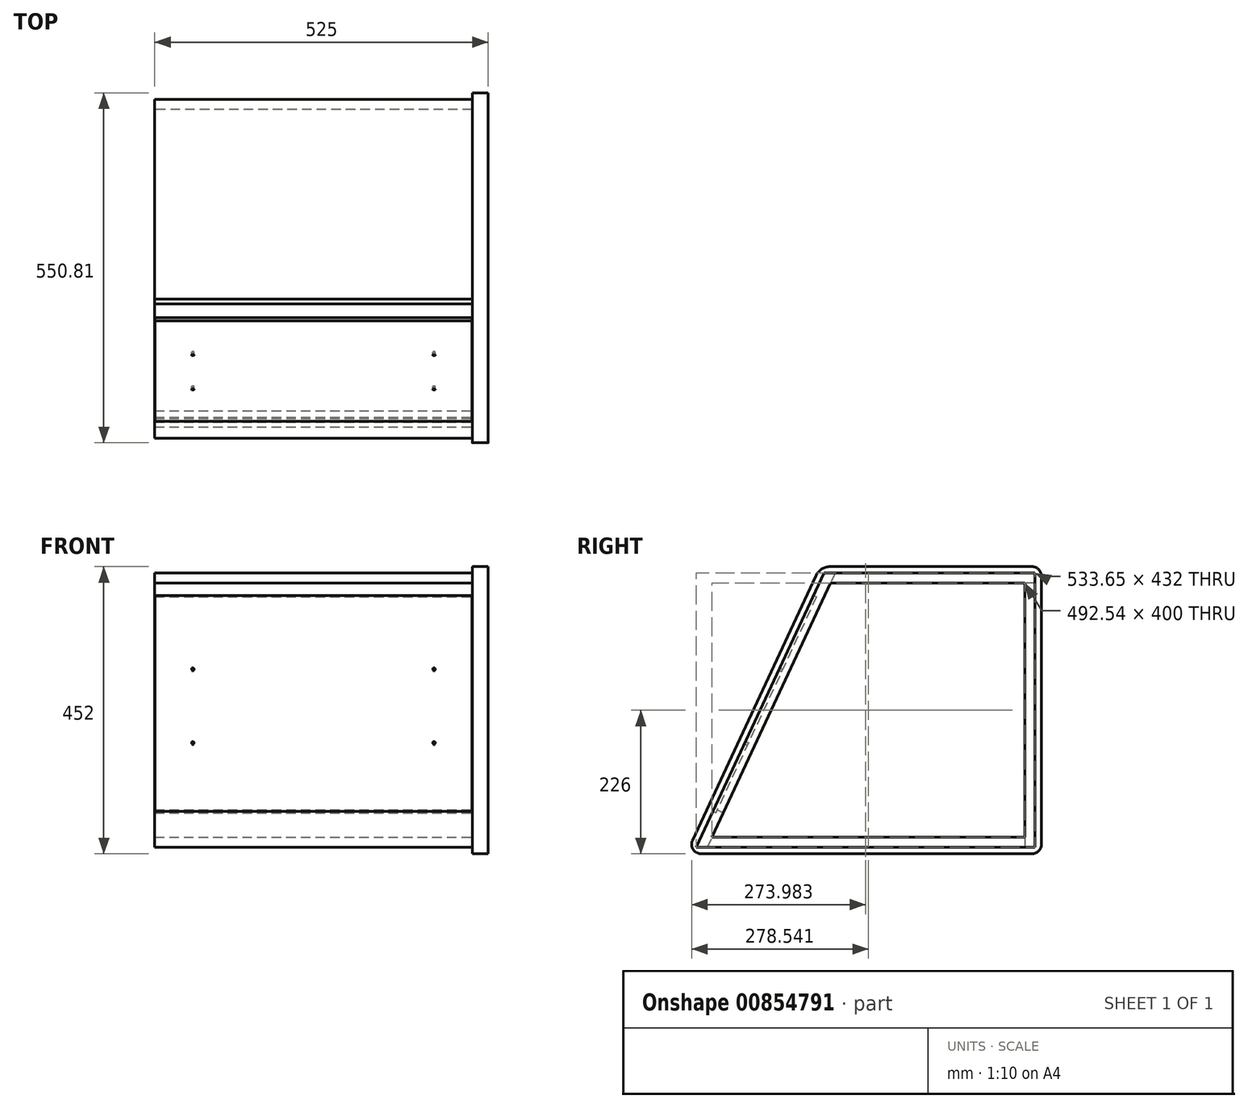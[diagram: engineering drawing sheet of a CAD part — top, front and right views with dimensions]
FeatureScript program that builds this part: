
annotation { "Feature Type Name" : "Feature", "Feature Type Description" : "" }
export const myFeature = defineFeature(function(context is Context, id is Id, definition is map)
    precondition{}
    {
        {
            var Q0;
            Q0=qCreatedBy(makeId("Top.planeOp"),FACE);
            var sketch = newSketch(context, id + "F0", { "sketchPlane" : qUnion([Q0])});
            skLineSegment(sketch, "E0.bottom", {"start": v(-250, 250) * mm, "end": v(250, 250) * mm});
            skLineSegment(sketch, "E0.top", {"start": v(-250, -250) * mm, "end": v(250, -250) * mm});
            skLineSegment(sketch, "E0.left", {"start": v(-250, 250) * mm, "end": v(-250, -250) * mm});
            skLineSegment(sketch, "E0.right", {"start": v(250, 250) * mm, "end": v(250, -250) * mm});
            skPoint(sketch, "E0.middle", {"position": v(0, 0) * mm});
            skSolve(sketch);
        }
        {
            var Q0;
            Q0 = qSketchRegion(id + "F0", true);
            extrude(context, id + "F1", {"entities" : qUnion([Q0]), "depth" : 16 * mm, "offsetDistance" : 25 * mm});
        }
        {
            var Q0;
            Q0=qCreatedBy(makeId("Front.planeOp"),FACE);
            cPlane(context, id + "F2", {"entities" : qUnion([Q0]), "cplaneType" : CPlaneType.OFFSET, "offset" : 250 * mm, "oppositeDirection" : true, "width" : 150 * mm, "height" : 150 * mm});
        }
        {
            var Q0;
            Q0=qCreatedBy(id+"F2.planeOp",FACE);
            var sketch = newSketch(context, id + "F3", { "sketchPlane" : qUnion([Q0])});
            skLineSegment(sketch, "E1.bottom", {"start": v(250, 416) * mm, "end": v(-250, 416) * mm});
            skLineSegment(sketch, "E1.top", {"start": v(250, 0) * mm, "end": v(-250, 0) * mm});
            skLineSegment(sketch, "E1.left", {"start": v(250, 416) * mm, "end": v(250, 0) * mm});
            skLineSegment(sketch, "E1.right", {"start": v(-250, 416) * mm, "end": v(-250, 0) * mm});
            skSolve(sketch);
        }
        {
            var Q0;
            Q0 = qSketchRegion(id + "F3", true);
            extrude(context, id + "F4", {"entities" : qUnion([Q0]), "oppositeDirection" : true, "depth" : 16 * mm, "offsetDistance" : 25 * mm});
        }
        {
            var Q0;
            Q0=makeQuery(id+"F1.opExtrude","CAP_EDGE",EDGE,{"disambiguationData":[OSD([sQuery(id+"F0.wireOp",EDGE,"E0.top")])],"isStart":false});
            chamfer(context, id + "F5", {"entities" : qUnion([Q0]), "chamferType" : ChamferType.OFFSET_ANGLE, "width" : 16 * mm, "oppositeDirection" : true, "angle" : 25 * degree, "tangentPropagation" : true});
        }
        {
            var Q0;
            Q0=makeQuery(id+"F1.opExtrude","SWEPT_FACE",FACE,{"disambiguationData":[OSD([sQuery(id+"F0.wireOp",EDGE,"E0.right")])]});
            var sketch = newSketch(context, id + "F6", { "sketchPlane" : qUnion([Q0])});
            skLineSegment(sketch, "E2", {"start": v(-250, 0) * mm, "end": v(-224.64, 54.38) * mm});
            skLineSegment(sketch, "E3", {"start": v(-224.64, 54.38) * mm, "end": v(-234.61, 59.03) * mm});
            skLineSegment(sketch, "E4", {"start": v(-241.26, 56.6) * mm, "end": v(-264.5, 6.76) * mm});
            skLineSegment(sketch, "E5", {"start": v(-264.5, 6.76) * mm, "end": v(-266.33, 2.85) * mm});
            skLineSegment(sketch, "E6", {"start": v(-250, 0) * mm, "end": v(-264.51, 0) * mm});
            skPoint(sketch, "E7.visualSharp", {"position": v(-267.65, 0) * mm});
            skLineSegment(sketch, "E8", {"start": v(-241.26, 56.6) * mm, "end": v(-236.73, 54.5) * mm});
            skLineSegment(sketch, "E9", {"start": v(-236.73, 54.5) * mm, "end": v(-234.61, 59.03) * mm});
            skLineSegment(sketch, "E10", {"start": v(-266.33, 2.85) * mm, "end": v(-267.65, 0) * mm});
            skLineSegment(sketch, "E11", {"start": v(-264.51, 0) * mm, "end": v(-267.65, 0) * mm});
            skSolve(sketch);
        }
        {
            var Q0;
            Q0 = qSketchRegion(id + "F6", true);
            var Q1;
            Q1=makeQuery(id+"F1.opExtrude","SWEPT_FACE",FACE,{"disambiguationData":[OSD([sQuery(id+"F0.wireOp",EDGE,"E0.left")])]});
            extrude(context, id + "F7", {"entities" : qUnion([Q0]), "endBound" : BoundingType.UP_TO_SURFACE, "oppositeDirection" : true, "depth" : 25 * mm, "endBoundEntityFace" : qUnion([Q1]), "offsetDistance" : 25 * mm});
        }
        {
            var Q0;
            Q0=makeQuery(id+"F4.opExtrude","SWEPT_FACE",FACE,{"disambiguationData":[OSD([sQuery(id+"F3.wireOp",EDGE,"E1.bottom")])]});
            var sketch = newSketch(context, id + "F8", { "sketchPlane" : qUnion([Q0])});
            skLineSegment(sketch, "E12.bottom", {"start": v(250, 266) * mm, "end": v(-250, 266) * mm});
            skLineSegment(sketch, "E12.top", {"start": v(250, -234) * mm, "end": v(-250, -234) * mm});
            skLineSegment(sketch, "E12.left", {"start": v(250, 266) * mm, "end": v(250, -234) * mm});
            skLineSegment(sketch, "E12.right", {"start": v(-250, 266) * mm, "end": v(-250, -234) * mm});
            skSolve(sketch);
        }
        {
            var Q0;
            Q0 = qSketchRegion(id + "F8", true);
            extrude(context, id + "F9", {"entities" : qUnion([Q0]), "depth" : 16 * mm, "offsetDistance" : 25 * mm});
        }
        {
            var Q0;
            Q0=makeQuery(id+"F9.opExtrude","SWEPT_FACE",FACE,{"disambiguationData":[OSD([sQuery(id+"F8.wireOp",EDGE,"E12.left")])]});
            var sketch = newSketch(context, id + "F10", { "sketchPlane" : qUnion([Q0])});
            skLineSegment(sketch, "E13", {"start": v(-250, 0) * mm, "end": v(3.35, 543.3) * mm, "construction": true});
            skLineSegment(sketch, "E14", {"start": v(-48.56, 432) * mm, "end": v(-70.18, 385.63) * mm});
            skLineSegment(sketch, "E15", {"start": v(-70.18, 385.63) * mm, "end": v(-80.15, 390.28) * mm});
            skLineSegment(sketch, "E16", {"start": v(-82.56, 396.93) * mm, "end": v(-70.25, 423.34) * mm});
            skLineSegment(sketch, "E17", {"start": v(-56.65, 432) * mm, "end": v(-48.56, 432) * mm});
            skLineSegment(sketch, "E18", {"start": v(-80.15, 390.28) * mm, "end": v(-78.03, 394.81) * mm});
            skLineSegment(sketch, "E19", {"start": v(-78.03, 394.81) * mm, "end": v(-82.56, 396.93) * mm});
            skPoint(sketch, "E20.visualSharp", {"position": v(-66.2, 432) * mm});
            skLineSegment(sketch, "E21", {"start": v(-56.65, 432) * mm, "end": v(-66.2, 432) * mm});
            skLineSegment(sketch, "E22", {"start": v(-70.25, 423.34) * mm, "end": v(-66.2, 432) * mm});
            skSolve(sketch);
        }
        {
            var Q0;
            Q0 = qSketchRegion(id + "F10", true);
            var Q1;
            Q1=makeQuery(id+"F9.opExtrude","SWEPT_FACE",FACE,{"disambiguationData":[OSD([sQuery(id+"F8.wireOp",EDGE,"E12.right")])]});
            extrude(context, id + "F11", {"entities" : qUnion([Q0]), "endBound" : BoundingType.UP_TO_SURFACE, "oppositeDirection" : true, "depth" : 25 * mm, "endBoundEntityFace" : qUnion([Q1]), "offsetDistance" : 25 * mm});
        }
        {
            var Q0;
            Q0=makeQuery(id+"F9.opExtrude","SWEPT_FACE",FACE,{"disambiguationData":[OSD([sQuery(id+"F8.wireOp",EDGE,"E12.left")])]});
            var sketch = newSketch(context, id + "F12", { "sketchPlane" : qUnion([Q0])});
            skLineSegment(sketch, "E23", {"start": v(-31.95, 467.62) * mm, "end": v(-78.7, 367.35) * mm});
            skLineSegment(sketch, "E24", {"start": v(-78.7, 367.35) * mm, "end": v(-288.16, 367.35) * mm});
            skLineSegment(sketch, "E25", {"start": v(-288.16, 367.35) * mm, "end": v(-288.16, 474.8) * mm});
            skLineSegment(sketch, "E26", {"start": v(-288.16, 474.8) * mm, "end": v(-31.95, 467.62) * mm});
            skSolve(sketch);
        }
        {
            var Q0;
            Q0 = qSketchRegion(id + "F12", true);
            extrude(context, id + "F13", {"entities" : qUnion([Q0]), "operationType" : NewBodyOperationType.REMOVE, "endBound" : BoundingType.THROUGH_ALL, "oppositeDirection" : true, "depth" : 25 * mm, "offsetDistance" : 25 * mm});
        }
        {
            var Q0;
            Q0=makeQuery(id+"F1.opExtrude","SWEPT_FACE",FACE,{"disambiguationData":[OSD([sQuery(id+"F0.wireOp",EDGE,"E0.right")])]});
            var sketch = newSketch(context, id + "F14", { "sketchPlane" : qUnion([Q0])});
            skLineSegment(sketch, "E27.bottom", {"start": v(276, 442) * mm, "end": v(-72.58, 442) * mm});
            skLineSegment(sketch, "E27.top", {"start": v(276, -10) * mm, "end": v(-283.35, -10) * mm});
            skLineSegment(sketch, "E27.left", {"start": v(276, 442) * mm, "end": v(276, -10) * mm});
            skLineSegment(sketch, "E28", {"start": v(-72.58, 442) * mm, "end": v(-283.35, -10) * mm});
            skSolve(sketch);
        }
        {
            var Q0;
            Q0 = qSketchRegion(id + "F14", true);
            extrude(context, id + "F15", {"entities" : qUnion([Q0]), "depth" : 25 * mm, "offsetDistance" : 25 * mm});
        }
        {
            var Q0;
            Q0=makeQuery(id+"F15.opExtrude","SWEPT_EDGE",EDGE,{"disambiguationData":[OSD([sQuery(id+"F14.wireOp",EDGE,"E27.top"),sQuery(id+"F14.wireOp",EDGE,"E27.left")])]});
            var Q1;
            Q1=makeQuery(id+"F15.opExtrude","SWEPT_EDGE",EDGE,{"disambiguationData":[OSD([sQuery(id+"F14.wireOp",EDGE,"E27.top"),sQuery(id+"F14.wireOp",EDGE,"E28")])]});
            fillet(context, id + "F16", {"entities" : qUnion([Q0, Q1]), "radius" : 15 * mm, "tangentPropagation" : true, "allowEdgeOverflow" : false});
        }
        {
            var Q0;
            Q0=makeQuery(id+"F15.opExtrude","SWEPT_EDGE",EDGE,{"disambiguationData":[OSD([sQuery(id+"F14.wireOp",EDGE,"E27.bottom"),sQuery(id+"F14.wireOp",EDGE,"E28")])]});
            fillet(context, id + "F17", {"entities" : qUnion([Q0]), "radius" : 25 * mm, "tangentPropagation" : true, "allowEdgeOverflow" : false});
        }
        {
            var Q0;
            Q0=makeQuery(id+"F15.opExtrude","SWEPT_EDGE",EDGE,{"disambiguationData":[OSD([sQuery(id+"F14.wireOp",EDGE,"E27.bottom"),sQuery(id+"F14.wireOp",EDGE,"E27.left")])]});
            fillet(context, id + "F18", {"entities" : qUnion([Q0]), "radius" : 15 * mm, "tangentPropagation" : true, "allowEdgeOverflow" : false});
        }
        {
            var Q0;
            Q0=makeQuery(id+"F15.opExtrude","CAP_FACE",FACE,{"disambiguationData":[OSD([sQuery(id+"F14.wireOp",EDGE,"E27.bottom"),sQuery(id+"F14.wireOp",EDGE,"E27.top"),sQuery(id+"F14.wireOp",EDGE,"E27.left"),sQuery(id+"F14.wireOp",EDGE,"E28")])],"isStart":true});
            var sketch = newSketch(context, id + "F19", { "sketchPlane" : qUnion([Q0])});
            skLineSegment(sketch, "E29", {"start": v(267.65, 0) * mm, "end": v(-266, 0) * mm});
            skLineSegment(sketch, "E30", {"start": v(-266, 0) * mm, "end": v(-266, 432) * mm});
            skLineSegment(sketch, "E31", {"start": v(-266, 432) * mm, "end": v(66.2, 432) * mm});
            skLineSegment(sketch, "E32", {"start": v(66.2, 432) * mm, "end": v(267.65, 0) * mm});
            skLineSegment(sketch, "E33", {"start": v(-250, 416) * mm, "end": v(-250, 16) * mm});
            skLineSegment(sketch, "E34", {"start": v(-250, 16) * mm, "end": v(242.54, 16) * mm});
            skLineSegment(sketch, "E35", {"start": v(242.54, 16) * mm, "end": v(56.02, 416) * mm});
            skLineSegment(sketch, "E36", {"start": v(56.02, 416) * mm, "end": v(-250, 416) * mm});
            skSolve(sketch);
        }
        {
            var Q0;
            Q0 = qSketchRegion(id + "F19", true);
            extrude(context, id + "F20", {"entities" : qUnion([Q0]), "operationType" : NewBodyOperationType.REMOVE, "oppositeDirection" : true, "depth" : 1 * mm, "offsetDistance" : 25 * mm});
        }
        {
            var Q0;
            Q0=makeQuery(id+"F7.opExtrude","SWEPT_FACE",FACE,{"disambiguationData":[OSD([sQuery(id+"F6.wireOp",EDGE,"E9")])]});
            var sketch = newSketch(context, id + "F21", { "sketchPlane" : qUnion([Q0])});
            skLineSegment(sketch, "E37.bottom", {"start": v(-249.8, 324.65) * mm, "end": v(249.8, 324.65) * mm});
            skLineSegment(sketch, "E37.top", {"start": v(-249.8, -50.45) * mm, "end": v(249.8, -50.45) * mm});
            skLineSegment(sketch, "E37.left", {"start": v(-249.8, 324.65) * mm, "end": v(-249.8, -50.45) * mm});
            skLineSegment(sketch, "E37.right", {"start": v(249.8, 324.65) * mm, "end": v(249.8, -50.45) * mm});
            skCircle(sketch, "E38", {"center": v(189.8, 196.65) * mm, "radius": 2 * mm});
            skCircle(sketch, "E39", {"center": v(189.8, 68.65) * mm, "radius": 2 * mm});
            skCircle(sketch, "E40", {"center": v(-190, 68.65) * mm, "radius": 2 * mm});
            skCircle(sketch, "E41", {"center": v(-190, 196.65) * mm, "radius": 2 * mm});
            skSolve(sketch);
        }
        {
            var Q0;
            Q0 = qSketchRegion(id + "F21", true);
            extrude(context, id + "F22", {"entities" : qUnion([Q0]), "depth" : 5 * mm, "offsetDistance" : 25 * mm});
        }
        {
            var Q0;
            Q0=makeQuery(id+"F15.opExtrude","CAP_FACE",FACE,{"disambiguationData":[OSD([sQuery(id+"F14.wireOp",EDGE,"E27.bottom"),sQuery(id+"F14.wireOp",EDGE,"E27.top"),sQuery(id+"F14.wireOp",EDGE,"E27.left"),sQuery(id+"F14.wireOp",EDGE,"E28")])],"isStart":false});
            var sketch = newSketch(context, id + "F23", { "sketchPlane" : qUnion([Q0])});
            skLineSegment(sketch, "E42", {"start": v(266, 432) * mm, "end": v(-66.2, 432) * mm});
            skLineSegment(sketch, "E43", {"start": v(-66.2, 432) * mm, "end": v(-267.65, 0) * mm});
            skLineSegment(sketch, "E44", {"start": v(-267.65, 0) * mm, "end": v(266, 0) * mm});
            skLineSegment(sketch, "E45", {"start": v(266, 0) * mm, "end": v(266, 432) * mm});
            skLineSegment(sketch, "E46", {"start": v(250, 416) * mm, "end": v(250, 16) * mm});
            skLineSegment(sketch, "E47", {"start": v(250, 16) * mm, "end": v(-242.54, 16) * mm});
            skLineSegment(sketch, "E48", {"start": v(-242.54, 16) * mm, "end": v(-56.02, 416) * mm});
            skLineSegment(sketch, "E49", {"start": v(-56.02, 416) * mm, "end": v(250, 416) * mm});
            skSolve(sketch);
        }
        {
            var Q0;
            Q0 = qSketchRegion(id + "F23", true);
            extrude(context, id + "F24", {"entities" : qUnion([Q0]), "operationType" : NewBodyOperationType.REMOVE, "oppositeDirection" : true, "depth" : 1 * mm, "offsetDistance" : 25 * mm});
        }
    });
